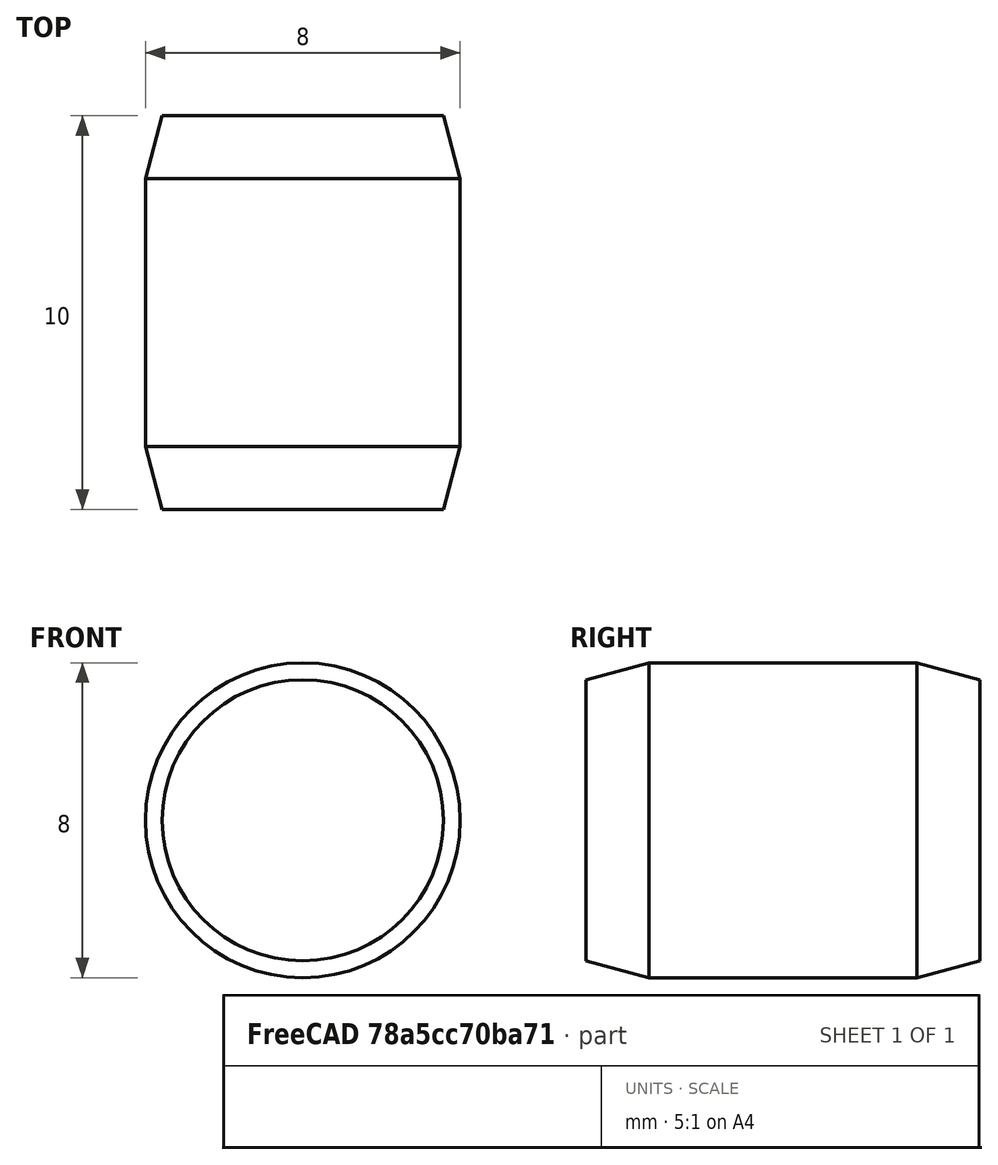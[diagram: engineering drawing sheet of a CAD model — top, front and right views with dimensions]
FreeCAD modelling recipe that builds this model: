
FCSTD DOCUMENT  (FreeCAD 0.15R4470 (Git))
Label: Zyl-Stift_ISO_2338-8x10
License: CC-BY 3.0
LicenseURL: http://creativecommons.org/licenses/by/3.0/
objects: Sketcher::SketchObject×1, PartDesign::Revolution×1
note: 3 computed .brp shape members not serialized (recipe doc carries the construction recipe); baked Part::Feature solids carry a one-line shape summary decoded from their .brp

FEATURE [Sketcher::SketchObject] Sketch
  Placement = pos=(0,0,0) rot=(0.57735,0.57735,0.57735;2.0944rad)
  sketch-geometry (7):
    g0: LineSegment StartX=0 StartY=0 StartZ=0 EndX=0 EndY=3.57128 EndZ=0
    g1: LineSegment StartX=0 StartY=3.57128 StartZ=0 EndX=1.6 EndY=4 EndZ=0
    g2: LineSegment StartX=1.6 StartY=4 StartZ=0 EndX=8.4 EndY=4 EndZ=0
    g3: LineSegment StartX=8.4 StartY=4 StartZ=0 EndX=10 EndY=3.57128 EndZ=0
    g4: LineSegment StartX=10 StartY=3.57128 StartZ=0 EndX=10 EndY=0 EndZ=0
    g5: LineSegment StartX=10 StartY=0 StartZ=0 EndX=0 EndY=0 EndZ=0
    g6: LineSegment [constr] StartX=0 StartY=3.57128 StartZ=0 EndX=10 EndY=3.57128 EndZ=0
  constraints (19):
    c: Coincident(g0,g-1)
    c: PointOnObject(g0,g-2)
    c: Coincident(g0,g1)
    c: Coincident(g1,g2)
    c: Horizontal(g2)
    c: Coincident(g2,g3)
    c: Coincident(g3,g4)
    c: Vertical(g4)
    c: Coincident(g4,g5)
    c: Coincident(g5,g-1)
    c: Horizontal(g5)
    c: Equal(g3,g1)
    c: Coincident(g6,g0)
    c: Coincident(g6,g3)
    c: Horizontal(g6)
    c: Angle(g6,g1) = 0.261799
    c: DistanceY(g-1,g1) = 4
    c: DistanceX(g5) = -10
    c: DistanceX(g1) = 1.6
FEATURE [PartDesign::Revolution] Revolution  label="Zyl-Stift ISO 2338-8x10 #"
  Angle = 360
  Axis = (0,1,0)
  Base = (0,0,0)
  Placement = pos=(0,0,0) rot=(0.57735,0.57735,0.57735;2.0944rad)
  ReferenceAxis = -> Sketch [H_Axis]
  Sketch = -> Sketch
